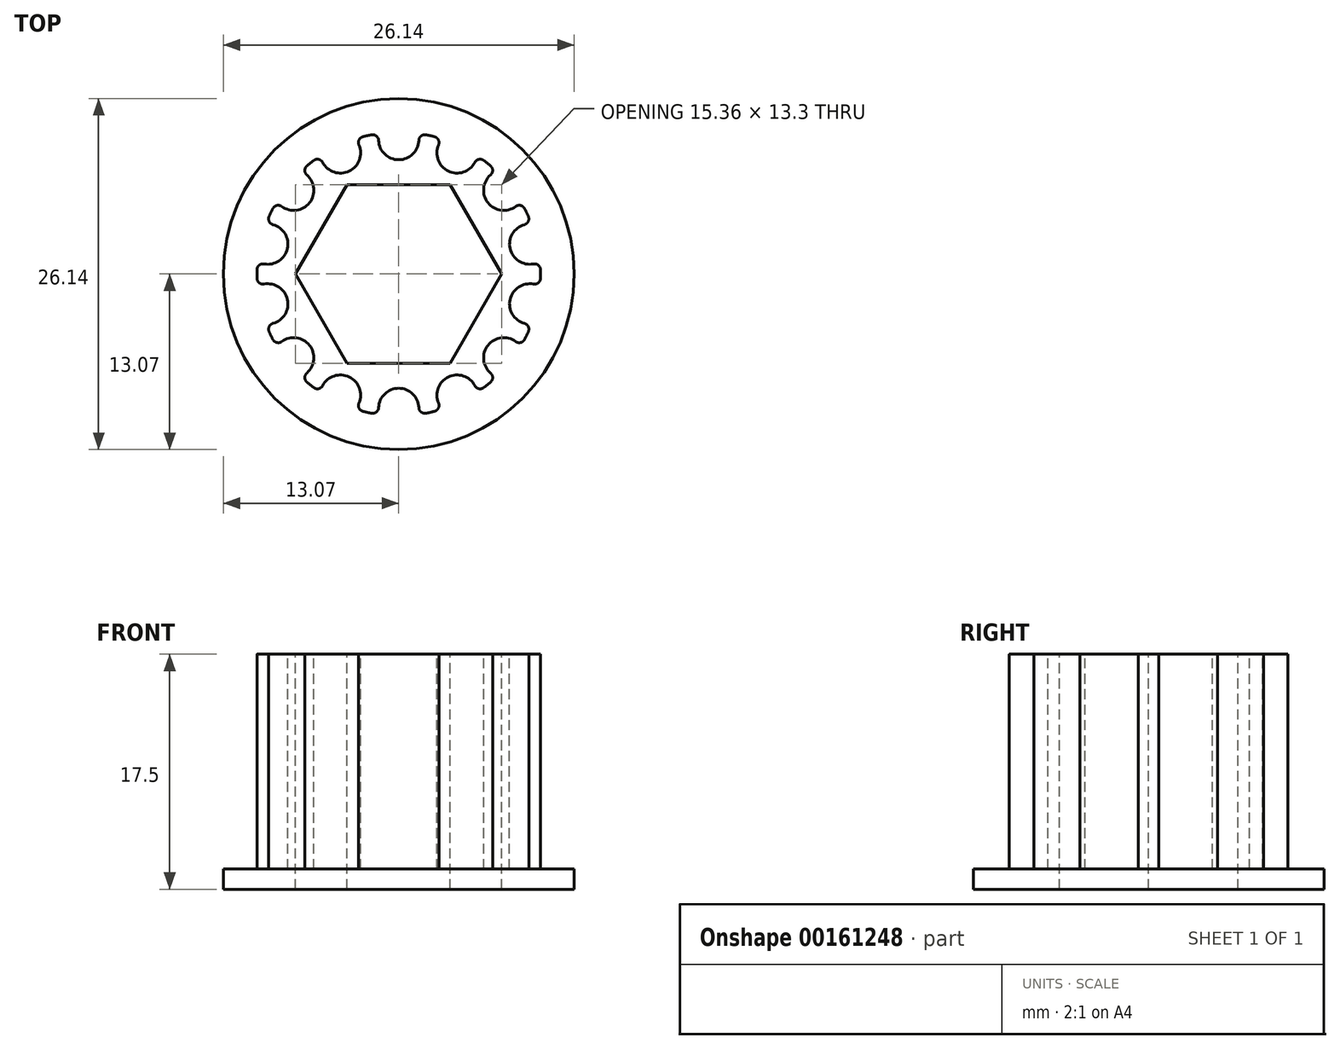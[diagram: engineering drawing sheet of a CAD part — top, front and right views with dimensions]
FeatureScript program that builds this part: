
annotation { "Feature Type Name" : "Feature", "Feature Type Description" : "" }
export const myFeature = defineFeature(function(context is Context, id is Id, definition is map)
    precondition{}
    {
        {
            assignVariable(context, id + "F0", {"name" : "Teeth", "anyValue" : 14});
        }
        {
            assignVariable(context, id + "F1", {"name" : "Width", "anyValue" : 16});
        }
        {
            var Q0;
            Q0=qCreatedBy(makeId("Top.planeOp"),FACE);
            var sketch = newSketch(context, id + "F2", { "sketchPlane" : qUnion([Q0])});
            skCircle(sketch, "E0", {"center": v(0, 0) * mm, "radius": 10.57 * mm});
            skSolve(sketch);
        }
        {
            var Q0;
            Q0=qSketchRegion(id+"F2",true);
            extrude(context, id + "F3", {"entities" : qUnion([Q0]), "depth" : (getVariable(context, 'Width')) * mm});
        }
        {
            var Q0;
            Q0=makeQuery(id+"F3.opExtrude","CAP_FACE",FACE,{"disambiguationData":[OSD([sQuery(id+"F2.wireOp",EDGE,"E0")])],"isStart":false});
            var sketch = newSketch(context, id + "F4", { "sketchPlane" : qUnion([Q0])});
            skCircle(sketch, "E1", {"center": v(0, 0) * mm, "radius": 8.5 * mm, "construction": true});
            skArc(sketch, "E2", {"start": v(-1.5, 9.95) * mm, "mid": v(0, 8.5) * mm, "end": v(1.5, 9.95) * mm});
            skArc(sketch, "E3", {"start": v(2.04, 10.37) * mm, "mid": v(0, 10.57) * mm, "end": v(-2.04, 10.37) * mm});
            skArc(sketch, "E4", {"start": v(-1.5, 9.95) * mm, "mid": v(-1.67, 10.28) * mm, "end": v(-2.04, 10.37) * mm});
            skArc(sketch, "E5", {"start": v(2.04, 10.37) * mm, "mid": v(1.67, 10.28) * mm, "end": v(1.5, 9.95) * mm});
            skSolve(sketch);
        }
        {
            var Q0;
            Q0=makeQuery(id+"F4.imprint","IMPRINT",FACE,{"disambiguationData":[TD([[makeQuery(id+"F4.imprint","IMPRINT",EDGE,{"derivedFrom":sQuery(id+"F4.wireOp",EDGE,"E2")}),1.0]])]});
            var Q1;
            Q1=makeQuery(id+"F3.opExtrude","CAP_FACE",FACE,{"disambiguationData":[OSD([sQuery(id+"F2.wireOp",EDGE,"E0")])],"isStart":true});
            extrude(context, id + "F5", {"entities" : qUnion([Q0]), "operationType" : NewBodyOperationType.REMOVE, "endBound" : BoundingType.UP_TO_SURFACE, "oppositeDirection" : true, "endBoundEntityFace" : qUnion([Q1]), "depth" : 25 * mm});
        }
        {
            var Q0;
            Q0=makeQuery(id+"F5.boolean.opBoolean","COPY",FACE,{"derivedFrom":makeQuery(id+"F5.opExtrude","SWEPT_FACE",FACE,{"disambiguationData":[OSD([sQuery(id+"F4.wireOp",EDGE,"E4")])]})});
            var Q1;
            Q1=makeQuery(id+"F5.boolean.opBoolean","COPY",FACE,{"derivedFrom":makeQuery(id+"F5.opExtrude","SWEPT_FACE",FACE,{"disambiguationData":[OSD([sQuery(id+"F4.wireOp",EDGE,"kHu0Iwj9-o4Cv-DRlk-4OjM-lw9Y4UkXsprA")])]})});
            var Q2;
            Q2=makeQuery(id+"F5.boolean.opBoolean","COPY",FACE,{"derivedFrom":makeQuery(id+"F5.opExtrude","SWEPT_FACE",FACE,{"disambiguationData":[OSD([sQuery(id+"F4.wireOp",EDGE,"E2")])]})});
            var Q3;
            Q3=makeQuery(id+"F5.boolean.opBoolean","COPY",FACE,{"derivedFrom":makeQuery(id+"F5.opExtrude","SWEPT_FACE",FACE,{"disambiguationData":[OSD([sQuery(id+"F4.wireOp",EDGE,"lCBZwTSR-BtAH-iuKv-YoZ4-wjcx4KIexOll")])]})});
            var Q4;
            Q4=makeQuery(id+"F5.boolean.opBoolean","COPY",FACE,{"derivedFrom":makeQuery(id+"F5.opExtrude","SWEPT_FACE",FACE,{"disambiguationData":[OSD([sQuery(id+"F4.wireOp",EDGE,"E5")])]})});
            var Q5;
            Q5=makeQuery(id+"F3.opExtrude","SWEPT_FACE",FACE,{"disambiguationData":[OSD([sQuery(id+"F2.wireOp",EDGE,"E0")])]});
            circularPattern(context, id + "F6", {"faces" : qUnion([Q0, Q1, Q2, Q3, Q4]), "axis" : qUnion([Q5]), "angle" : 360 * degree, "instanceCount" : getVariable(context, 'Teeth'), "equalSpace" : true, "patternType" : PatternType.FACE});
        }
        {
            var Q0;
            Q0=makeQuery(id+"F3.opExtrude","CAP_FACE",FACE,{"disambiguationData":[OSD([sQuery(id+"F2.wireOp",EDGE,"E0")])],"isStart":false});
            var sketch = newSketch(context, id + "F7", { "sketchPlane" : qUnion([Q0])});
            skCircle(sketch, "E6.cCircle", {"center": v(0, 0) * mm, "radius": 6.65 * mm, "construction": true});
            skLineSegment(sketch, "E6.0", {"start": v(-3.84, 6.65) * mm, "end": v(3.84, 6.65) * mm});
            skLineSegment(sketch, "E6.1", {"start": v(3.84, 6.65) * mm, "end": v(7.68, 0) * mm});
            skLineSegment(sketch, "E6.2", {"start": v(7.68, 0) * mm, "end": v(3.84, -6.65) * mm});
            skLineSegment(sketch, "E6.3", {"start": v(3.84, -6.65) * mm, "end": v(-3.84, -6.65) * mm});
            skLineSegment(sketch, "E6.4", {"start": v(-3.84, -6.65) * mm, "end": v(-7.68, 0) * mm});
            skLineSegment(sketch, "E6.5", {"start": v(-7.68, 0) * mm, "end": v(-3.84, 6.65) * mm});
            skPoint(sketch, "E6.0.midPoint", {"position": v(0, 6.65) * mm});
            skSolve(sketch);
        }
        {
            var Q0;
            Q0=makeQuery(id+"F2.imprint","IMPRINT",FACE,{"disambiguationData":[TD([[makeQuery(id+"F2.imprint","IMPRINT",EDGE,{"derivedFrom":sQuery(id+"F2.wireOp",EDGE,"E0")}),1.0]])]});
            var sketch = newSketch(context, id + "F8", { "sketchPlane" : qUnion([Q0])});
            skCircle(sketch, "E7.0", {"center": v(0, 0) * mm, "radius": 10.57 * mm, "construction": true});
            skCircle(sketch, "E8", {"center": v(0, 0) * mm, "radius": 13.07 * mm});
            skSolve(sketch);
        }
        {
            var Q0;
            Q0=makeQuery(id+"F8.imprint","IMPRINT",FACE,{"disambiguationData":[TD([[makeQuery(id+"F8.imprint","IMPRINT",EDGE,{"derivedFrom":sQuery(id+"F8.wireOp",EDGE,"E8")}),1.0]])]});
            var Q1;
            Q1=makeQuery(id+"F2.imprint","IMPRINT",FACE,{"disambiguationData":[TD([[makeQuery(id+"F2.imprint","IMPRINT",EDGE,{"derivedFrom":sQuery(id+"F2.wireOp",EDGE,"E0")}),1.0]])]});
            extrude(context, id + "F9", {"entities" : qUnion([Q0, Q1]), "operationType" : NewBodyOperationType.ADD, "oppositeDirection" : true, "depth" : 1.5 * mm});
        }
        {
            var Q0;
            Q0=makeQuery(id+"F7.imprint","IMPRINT",FACE,{"disambiguationData":[TD([[makeQuery(id+"F7.imprint","IMPRINT",EDGE,{"derivedFrom":sQuery(id+"F7.wireOp",EDGE,"E6.0")}),-1.0]])]});
            extrude(context, id + "F10", {"entities" : qUnion([Q0]), "operationType" : NewBodyOperationType.REMOVE, "endBound" : BoundingType.THROUGH_ALL, "oppositeDirection" : true, "depth" : 25 * mm});
        }
    });
